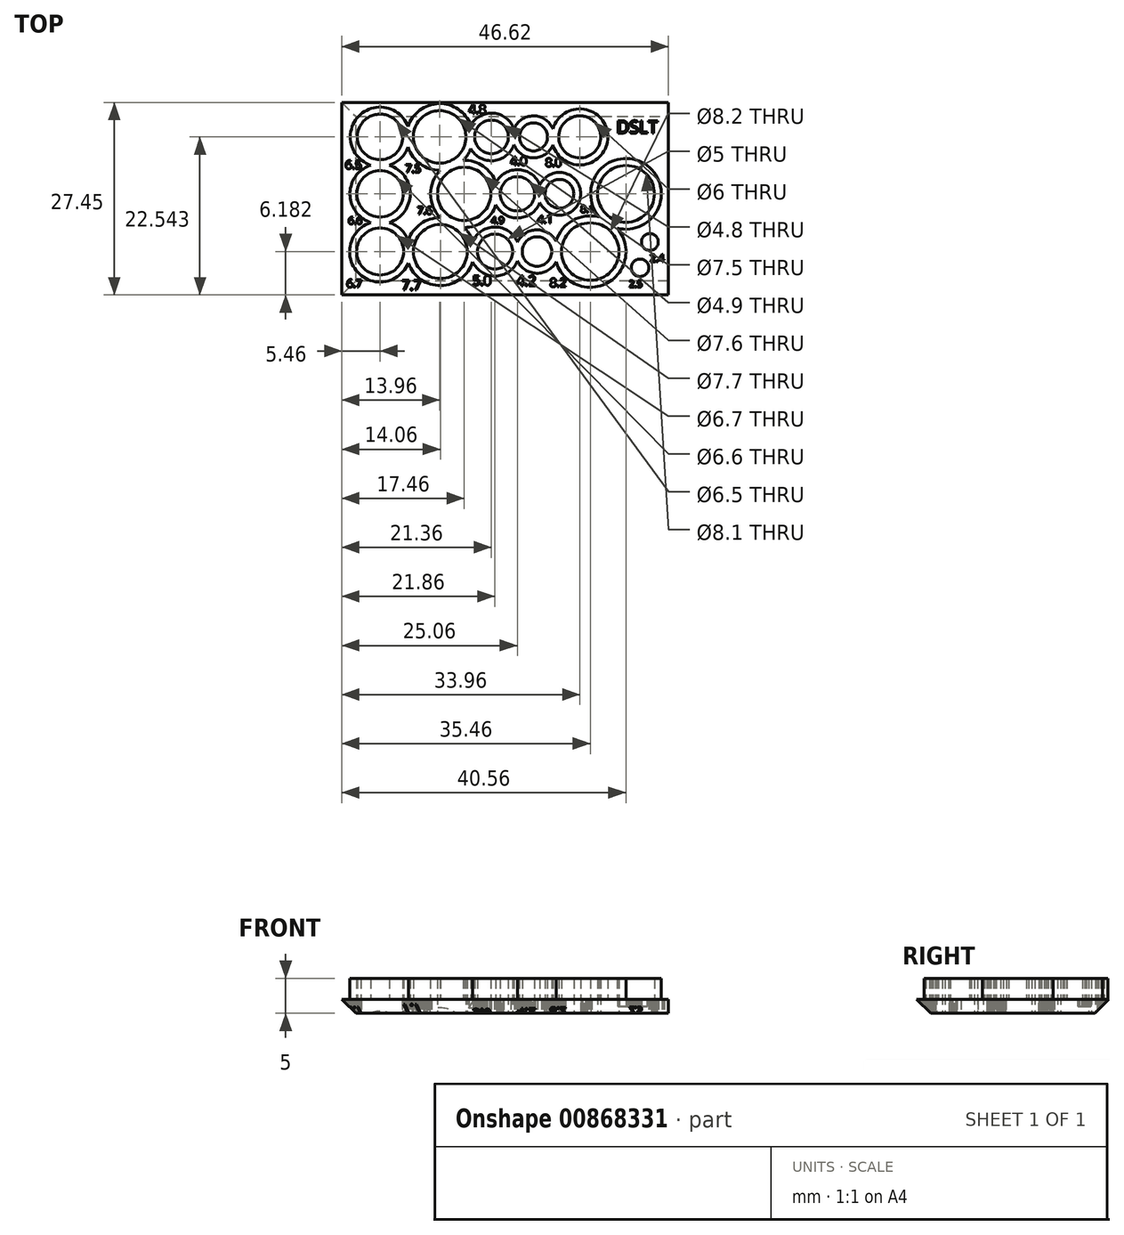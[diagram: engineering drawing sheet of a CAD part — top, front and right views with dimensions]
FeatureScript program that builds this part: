
annotation { "Feature Type Name" : "Feature", "Feature Type Description" : "" }
export const myFeature = defineFeature(function(context is Context, id is Id, definition is map)
    precondition{}
    {
        {
            var Q0;
            Q0=qCreatedBy(makeId("Top.planeOp"),FACE);
            var sketch = newSketch(context, id + "F0", { "sketchPlane" : qUnion([Q0])});
            skCircle(sketch, "E0", {"center": v(0, 0) * mm, "radius": 3.3 * mm});
            skLineSegment(sketch, "E1", {"start": v(0, 0) * mm, "end": v(43.8, 0) * mm, "construction": true});
            skLineSegment(sketch, "E2", {"start": v(0, 8.12) * mm, "end": v(43.8, 8.12) * mm, "construction": true});
            skCircle(sketch, "E3", {"center": v(0, 8.12) * mm, "radius": 3.25 * mm});
            skCircle(sketch, "E4", {"center": v(0, -8.24) * mm, "radius": 3.35 * mm});
            skLineSegment(sketch, "E5", {"start": v(0, -8.24) * mm, "end": v(43.8, -8.24) * mm, "construction": true});
            skCircle(sketch, "E6", {"center": v(12, 0) * mm, "radius": 3.8 * mm});
            skCircle(sketch, "E7", {"center": v(8.6, -8.24) * mm, "radius": 3.85 * mm});
            skCircle(sketch, "E8", {"center": v(8.5, 8.12) * mm, "radius": 3.75 * mm});
            skCircle(sketch, "E9", {"center": v(19.6, 0) * mm, "radius": 2.45 * mm});
            skCircle(sketch, "E10", {"center": v(15.9, 8.12) * mm, "radius": 2.4 * mm});
            skCircle(sketch, "E11", {"center": v(16.4, -8.24) * mm, "radius": 2.5 * mm});
            skCircle(sketch, "E12", {"center": v(25.6, 0) * mm, "radius": 2.05 * mm});
            skCircle(sketch, "E13", {"center": v(21.9, 8.12) * mm, "radius": 2 * mm});
            skCircle(sketch, "E14", {"center": v(22.4, -8.24) * mm, "radius": 2.1 * mm});
            skCircle(sketch, "E15", {"center": v(35.1, 0) * mm, "radius": 4.05 * mm});
            skCircle(sketch, "E16", {"center": v(30, -8.24) * mm, "radius": 4.1 * mm});
            skCircle(sketch, "E17", {"center": v(28.5, 8.12) * mm, "radius": 4 * mm});
            skCircle(sketch, "E18.0", {"center": v(0, 8.12) * mm, "radius": 4.25 * mm});
            skCircle(sketch, "E19.0", {"center": v(0, 0) * mm, "radius": 4.3 * mm});
            skCircle(sketch, "E20.0", {"center": v(0, -8.24) * mm, "radius": 4.35 * mm});
            skCircle(sketch, "E21.0", {"center": v(8.5, 8.12) * mm, "radius": 4.75 * mm});
            skCircle(sketch, "E22.0", {"center": v(12, 0) * mm, "radius": 4.8 * mm});
            skCircle(sketch, "E23.0", {"center": v(8.6, -8.24) * mm, "radius": 4.85 * mm});
            skCircle(sketch, "E24.0", {"center": v(15.9, 8.12) * mm, "radius": 3.4 * mm});
            skCircle(sketch, "E25.0", {"center": v(19.6, 0) * mm, "radius": 3.45 * mm});
            skCircle(sketch, "E26.0", {"center": v(16.4, -8.24) * mm, "radius": 3.5 * mm});
            skCircle(sketch, "E27.0", {"center": v(21.9, 8.12) * mm, "radius": 3 * mm});
            skCircle(sketch, "E28.0", {"center": v(25.6, 0) * mm, "radius": 3.05 * mm});
            skCircle(sketch, "E29.0", {"center": v(22.4, -8.24) * mm, "radius": 3.1 * mm});
            skCircle(sketch, "E30.0", {"center": v(30, -8.24) * mm, "radius": 5.1 * mm});
            skCircle(sketch, "E31.0", {"center": v(28.5, 8.12) * mm, "radius": 3 * mm});
            skCircle(sketch, "E32.0", {"center": v(35.1, 0) * mm, "radius": 5.05 * mm});
            skLineSegment(sketch, "E33.bottom", {"start": v(-5.46, 13.03) * mm, "end": v(41.16, 13.03) * mm});
            skLineSegment(sketch, "E33.top", {"start": v(-5.46, -14.42) * mm, "end": v(41.16, -14.42) * mm});
            skLineSegment(sketch, "E33.left", {"start": v(-5.46, 13.03) * mm, "end": v(-5.46, -14.42) * mm});
            skLineSegment(sketch, "E33.right", {"start": v(41.16, 13.03) * mm, "end": v(41.16, -14.42) * mm});
            skText(sketch, "E34", { "text": "6.6", "fontName": "OpenSans-Regular.ttf"});
            skText(sketch, "E35", { "text": "7.6", "fontName": "OpenSans-Regular.ttf"});
            skText(sketch, "E36", { "text": "4.9\n", "fontName": "OpenSans-Regular.ttf"});
            skText(sketch, "E37", { "text": "4.1", "fontName": "OpenSans-Regular.ttf"});
            skText(sketch, "E38", { "text": "8.1", "fontName": "OpenSans-Regular.ttf"});
            skText(sketch, "E39", { "text": "6.5", "fontName": "OpenSans-Regular.ttf"});
            skText(sketch, "E40", { "text": "7.5", "fontName": "OpenSans-Regular.ttf"});
            skText(sketch, "E41", { "text": "4.8", "fontName": "OpenSans-Regular.ttf"});
            skText(sketch, "E42", { "text": "4.0", "fontName": "OpenSans-Regular.ttf"});
            skText(sketch, "E43", { "text": "8.0", "fontName": "OpenSans-Regular.ttf"});
            skText(sketch, "E44", { "text": "6.7", "fontName": "OpenSans-Regular.ttf"});
            skText(sketch, "E45", { "text": "7.7", "fontName": "OpenSans-Regular.ttf"});
            skText(sketch, "E46", { "text": "5.0", "fontName": "OpenSans-Regular.ttf"});
            skText(sketch, "E47", { "text": "8.2", "fontName": "OpenSans-Regular.ttf"});
            skText(sketch, "E48", { "text": "4.2", "fontName": "OpenSans-Regular.ttf"});
            skCircle(sketch, "E49", {"center": v(37.1, -10.55) * mm, "radius": 1.25 * mm});
            skCircle(sketch, "E50", {"center": v(38.5, -6.87) * mm, "radius": 1.2 * mm});
            skText(sketch, "E51", { "text": "2.5\n", "fontName": "OpenSans-Regular.ttf"});
            skText(sketch, "E52", { "text": "2.4\n", "fontName": "OpenSans-Regular.ttf"});
            const initialGuessF0  = {"E34": [-0.00453, -0.00432, 1, 0, 0.001], "E35": [0.00531, -0.0029, 1, 0, 0.00108], "E36": [0.01582, -0.00425, 1, 0, 0.00096], "E37": [0.02247, -0.00417, 1, 0, 0.0011], "E38": [0.02863, -0.00266, 1, 0, 0.00098], "E39": [-0.00498, 0.00356, 1, 0, 0.0012], "E40": [0.0036, 0.00304, 1, 0, 0.00114], "E41": [0.01265, 0.01143, 1, 0, 0.00126], "E42": [0.0186, 0.00408, 1, 0, 0.0012], "E43": [0.02362, 0.0039, 1, 0, 0.00116], "E44": [-0.00477, -0.01334, 1, 0, 0.00112], "E45": [0.00307, -0.01373, 1, 0, 0.00145], "E46": [0.01322, -0.01303, 1, 0, 0.00135], "E47": [0.02424, -0.01327, 1, 0, 0.0012], "E48": [0.01949, -0.01311, 1, 0, 0.00142], "E51": [0.03552, -0.01333, 1, 0, 0.00098], "E52": [0.0385, -0.0097, 1, 0, 0.00107]};
            skSetInitialGuess(sketch, initialGuessF0);
            skSolve(sketch);
        }
        {
            var Q0;
            Q0=makeQuery(id+"F0.imprint","IMPRINT",FACE,{"disambiguationData":[TD([[makeQuery(id+"F0.imprint","IMPRINT",EDGE,{"derivedFrom":sQuery(id+"F0.wireOp",EDGE,"E3")}),-1.0]])]});
            var Q1;
            {var subQ0=sQuery(id+"F0.wireOp",EDGE,"E19.0");var subQ1=sQuery(id+"F0.wireOp",EDGE,"E18.0");var subQ2=makeQuery(id+"F0.imprint","INTERSECT",VERTEX,{"disambiguationData":[OD(0.0)],"derivedFrom":[subQ1,subQ0]});Q1=makeQuery(id+"F0.imprint","IMPRINT",FACE,{"disambiguationData":[TD([[makeQuery(id+"F0.imprint","IMPRINT",EDGE,{"disambiguationData":[TD([[subQ2,-1.0]])],"derivedFrom":subQ1}),1.0]])]});}
            var Q2;
            Q2=makeQuery(id+"F0.imprint","IMPRINT",FACE,{"disambiguationData":[TD([[makeQuery(id+"F0.imprint","IMPRINT",EDGE,{"derivedFrom":sQuery(id+"F0.wireOp",EDGE,"E0")}),-1.0]])]});
            var Q3;
            {var subQ0=sQuery(id+"F0.wireOp",EDGE,"E20.0");var subQ1=sQuery(id+"F0.wireOp",EDGE,"E19.0");var subQ2=makeQuery(id+"F0.imprint","INTERSECT",VERTEX,{"disambiguationData":[OD(0.0)],"derivedFrom":[subQ1,subQ0]});Q3=makeQuery(id+"F0.imprint","IMPRINT",FACE,{"disambiguationData":[TD([[makeQuery(id+"F0.imprint","IMPRINT",EDGE,{"disambiguationData":[TD([[subQ2,-1.0]])],"derivedFrom":subQ1}),1.0]])]});}
            var Q4;
            {var subQ0=sQuery(id+"F0.wireOp",EDGE,"E23.0");var subQ1=sQuery(id+"F0.wireOp",EDGE,"E20.0");var subQ2=makeQuery(id+"F0.imprint","INTERSECT",VERTEX,{"disambiguationData":[OD(0.0)],"derivedFrom":[subQ1,subQ0]});Q4=makeQuery(id+"F0.imprint","IMPRINT",FACE,{"disambiguationData":[TD([[makeQuery(id+"F0.imprint","IMPRINT",EDGE,{"disambiguationData":[TD([[subQ2,-1.0]])],"derivedFrom":subQ1}),1.0]])]});}
            var Q5;
            Q5=makeQuery(id+"F0.imprint","IMPRINT",FACE,{"disambiguationData":[TD([[makeQuery(id+"F0.imprint","IMPRINT",EDGE,{"derivedFrom":sQuery(id+"F0.wireOp",EDGE,"E7")}),-1.0]])]});
            var Q6;
            Q6=makeQuery(id+"F0.imprint","IMPRINT",FACE,{"disambiguationData":[TD([[makeQuery(id+"F0.imprint","IMPRINT",EDGE,{"derivedFrom":sQuery(id+"F0.wireOp",EDGE,"E6")}),-1.0]])]});
            var Q7;
            {var subQ0=sQuery(id+"F0.wireOp",EDGE,"E23.0");var subQ1=sQuery(id+"F0.wireOp",EDGE,"E22.0");var subQ2=makeQuery(id+"F0.imprint","INTERSECT",VERTEX,{"disambiguationData":[OD(0.0)],"derivedFrom":[subQ1,subQ0]});Q7=makeQuery(id+"F0.imprint","IMPRINT",FACE,{"disambiguationData":[TD([[makeQuery(id+"F0.imprint","IMPRINT",EDGE,{"disambiguationData":[TD([[subQ2,1.0]])],"derivedFrom":subQ1}),1.0]])]});}
            var Q8;
            {var subQ0=sQuery(id+"F0.wireOp",EDGE,"E22.0");var subQ1=sQuery(id+"F0.wireOp",EDGE,"E21.0");var subQ2=makeQuery(id+"F0.imprint","INTERSECT",VERTEX,{"disambiguationData":[OD(0.0)],"derivedFrom":[subQ1,subQ0]});Q8=makeQuery(id+"F0.imprint","IMPRINT",FACE,{"disambiguationData":[TD([[makeQuery(id+"F0.imprint","IMPRINT",EDGE,{"disambiguationData":[TD([[subQ2,1.0]])],"derivedFrom":subQ1}),1.0]])]});}
            var Q9;
            Q9=makeQuery(id+"F0.imprint","IMPRINT",FACE,{"disambiguationData":[TD([[makeQuery(id+"F0.imprint","IMPRINT",EDGE,{"derivedFrom":sQuery(id+"F0.wireOp",EDGE,"E8")}),-1.0]])]});
            var Q10;
            {var subQ0=sQuery(id+"F0.wireOp",EDGE,"E24.0");var subQ1=sQuery(id+"F0.wireOp",EDGE,"E21.0");var subQ2=makeQuery(id+"F0.imprint","INTERSECT",VERTEX,{"disambiguationData":[OD(0.0)],"derivedFrom":[subQ1,subQ0]});Q10=makeQuery(id+"F0.imprint","IMPRINT",FACE,{"disambiguationData":[TD([[makeQuery(id+"F0.imprint","IMPRINT",EDGE,{"disambiguationData":[TD([[subQ2,1.0]])],"derivedFrom":subQ1}),1.0]])]});}
            var Q11;
            Q11=makeQuery(id+"F0.imprint","IMPRINT",FACE,{"disambiguationData":[TD([[makeQuery(id+"F0.imprint","IMPRINT",EDGE,{"derivedFrom":sQuery(id+"F0.wireOp",EDGE,"E10")}),-1.0]])]});
            var Q12;
            {var subQ0=sQuery(id+"F0.wireOp",EDGE,"E27.0");var subQ1=sQuery(id+"F0.wireOp",EDGE,"E24.0");var subQ2=makeQuery(id+"F0.imprint","INTERSECT",VERTEX,{"disambiguationData":[OD(0.0)],"derivedFrom":[subQ1,subQ0]});Q12=makeQuery(id+"F0.imprint","IMPRINT",FACE,{"disambiguationData":[TD([[makeQuery(id+"F0.imprint","IMPRINT",EDGE,{"disambiguationData":[TD([[subQ2,1.0]])],"derivedFrom":subQ1}),1.0]])]});}
            var Q13;
            Q13=makeQuery(id+"F0.imprint","IMPRINT",FACE,{"disambiguationData":[TD([[makeQuery(id+"F0.imprint","IMPRINT",EDGE,{"derivedFrom":sQuery(id+"F0.wireOp",EDGE,"E13")}),-1.0]])]});
            var Q14;
            Q14=makeQuery(id+"F0.imprint","IMPRINT",FACE,{"disambiguationData":[TD([[makeQuery(id+"F0.imprint","IMPRINT",EDGE,{"derivedFrom":sQuery(id+"F0.wireOp",EDGE,"E9")}),-1.0]])]});
            var Q15;
            {var subQ0=sQuery(id+"F0.wireOp",EDGE,"E25.0");var subQ1=sQuery(id+"F0.wireOp",EDGE,"E22.0");var subQ2=makeQuery(id+"F0.imprint","INTERSECT",VERTEX,{"disambiguationData":[OD(0.0)],"derivedFrom":[subQ1,subQ0]});Q15=makeQuery(id+"F0.imprint","IMPRINT",FACE,{"disambiguationData":[TD([[makeQuery(id+"F0.imprint","IMPRINT",EDGE,{"disambiguationData":[TD([[subQ2,1.0]])],"derivedFrom":subQ1}),1.0]])]});}
            var Q16;
            {var subQ0=sQuery(id+"F0.wireOp",EDGE,"E26.0");var subQ1=sQuery(id+"F0.wireOp",EDGE,"E23.0");var subQ2=makeQuery(id+"F0.imprint","INTERSECT",VERTEX,{"disambiguationData":[OD(0.0)],"derivedFrom":[subQ1,subQ0]});Q16=makeQuery(id+"F0.imprint","IMPRINT",FACE,{"disambiguationData":[TD([[makeQuery(id+"F0.imprint","IMPRINT",EDGE,{"disambiguationData":[TD([[subQ2,1.0]])],"derivedFrom":subQ1}),1.0]])]});}
            var Q17;
            Q17=makeQuery(id+"F0.imprint","IMPRINT",FACE,{"disambiguationData":[TD([[makeQuery(id+"F0.imprint","IMPRINT",EDGE,{"derivedFrom":sQuery(id+"F0.wireOp",EDGE,"E11")}),-1.0]])]});
            var Q18;
            {var subQ0=sQuery(id+"F0.wireOp",EDGE,"E29.0");var subQ1=sQuery(id+"F0.wireOp",EDGE,"E26.0");var subQ2=makeQuery(id+"F0.imprint","INTERSECT",VERTEX,{"disambiguationData":[OD(0.0)],"derivedFrom":[subQ1,subQ0]});Q18=makeQuery(id+"F0.imprint","IMPRINT",FACE,{"disambiguationData":[TD([[makeQuery(id+"F0.imprint","IMPRINT",EDGE,{"disambiguationData":[TD([[subQ2,1.0]])],"derivedFrom":subQ1}),1.0]])]});}
            var Q19;
            Q19=makeQuery(id+"F0.imprint","IMPRINT",FACE,{"disambiguationData":[TD([[makeQuery(id+"F0.imprint","IMPRINT",EDGE,{"derivedFrom":sQuery(id+"F0.wireOp",EDGE,"E14")}),-1.0]])]});
            var Q20;
            {var subQ0=sQuery(id+"F0.wireOp",EDGE,"E28.0");var subQ1=sQuery(id+"F0.wireOp",EDGE,"E25.0");var subQ2=makeQuery(id+"F0.imprint","INTERSECT",VERTEX,{"disambiguationData":[OD(0.0)],"derivedFrom":[subQ1,subQ0]});Q20=makeQuery(id+"F0.imprint","IMPRINT",FACE,{"disambiguationData":[TD([[makeQuery(id+"F0.imprint","IMPRINT",EDGE,{"disambiguationData":[TD([[subQ2,1.0]])],"derivedFrom":subQ1}),1.0]])]});}
            var Q21;
            Q21=makeQuery(id+"F0.imprint","IMPRINT",FACE,{"disambiguationData":[TD([[makeQuery(id+"F0.imprint","IMPRINT",EDGE,{"derivedFrom":sQuery(id+"F0.wireOp",EDGE,"E12")}),-1.0]])]});
            var Q22;
            Q22=makeQuery(id+"F0.imprint","IMPRINT",FACE,{"disambiguationData":[TD([[makeQuery(id+"F0.imprint","IMPRINT",EDGE,{"derivedFrom":sQuery(id+"F0.wireOp",EDGE,"E16")}),-1.0]])]});
            var Q23;
            {var subQ0=sQuery(id+"F0.wireOp",EDGE,"E30.0");var subQ1=sQuery(id+"F0.wireOp",EDGE,"E29.0");var subQ2=makeQuery(id+"F0.imprint","INTERSECT",VERTEX,{"disambiguationData":[OD(0.0)],"derivedFrom":[subQ1,subQ0]});Q23=makeQuery(id+"F0.imprint","IMPRINT",FACE,{"disambiguationData":[TD([[makeQuery(id+"F0.imprint","IMPRINT",EDGE,{"disambiguationData":[TD([[subQ2,1.0]])],"derivedFrom":subQ1}),1.0]])]});}
            var Q24;
            {var subQ0=sQuery(id+"F0.wireOp",EDGE,"E32.0");var subQ1=sQuery(id+"F0.wireOp",EDGE,"E30.0");var subQ2=makeQuery(id+"F0.imprint","INTERSECT",VERTEX,{"disambiguationData":[OD(0.0)],"derivedFrom":[subQ1,subQ0]});Q24=makeQuery(id+"F0.imprint","IMPRINT",FACE,{"disambiguationData":[TD([[makeQuery(id+"F0.imprint","IMPRINT",EDGE,{"disambiguationData":[TD([[subQ2,1.0]])],"derivedFrom":subQ1}),1.0]])]});}
            var Q25;
            Q25=makeQuery(id+"F0.imprint","IMPRINT",FACE,{"disambiguationData":[TD([[makeQuery(id+"F0.imprint","IMPRINT",EDGE,{"derivedFrom":sQuery(id+"F0.wireOp",EDGE,"E15")}),-1.0]])]});
            var Q26;
            {var subQ0=sQuery(id+"F0.wireOp",EDGE,"E27.0");var subQ1=sQuery(id+"F0.wireOp",EDGE,"E17");var subQ2=makeQuery(id+"F0.imprint","INTERSECT",VERTEX,{"disambiguationData":[OD(0.0)],"derivedFrom":[subQ1,subQ0]});Q26=makeQuery(id+"F0.imprint","IMPRINT",FACE,{"disambiguationData":[TD([[makeQuery(id+"F0.imprint","IMPRINT",EDGE,{"disambiguationData":[TD([[subQ2,-1.0]])],"derivedFrom":subQ1}),1.0]])]});}
            var Q27;
            Q27=makeQuery(id+"F0.imprint","IMPRINT",FACE,{"disambiguationData":[TD([[makeQuery(id+"F0.imprint","IMPRINT",EDGE,{"derivedFrom":sQuery(id+"F0.wireOp",EDGE,"E31.0")}),-1.0]])]});
            var Q28;
            {var subQ0=sQuery(id+"F0.wireOp",EDGE,"E21.0");var subQ1=sQuery(id+"F0.wireOp",EDGE,"E18.0");var subQ2=makeQuery(id+"F0.imprint","INTERSECT",VERTEX,{"disambiguationData":[OD(0.0)],"derivedFrom":[subQ1,subQ0]});Q28=makeQuery(id+"F0.imprint","IMPRINT",FACE,{"disambiguationData":[TD([[makeQuery(id+"F0.imprint","IMPRINT",EDGE,{"disambiguationData":[TD([[subQ2,1.0]])],"derivedFrom":subQ1}),1.0]])]});}
            var Q29;
            Q29=makeQuery(id+"F0.imprint","IMPRINT",FACE,{"disambiguationData":[TD([[makeQuery(id+"F0.imprint","IMPRINT",EDGE,{"derivedFrom":sQuery(id+"F0.wireOp",EDGE,"E4")}),-1.0]])]});
            var Q30;
            {var subQ0=sQuery(id+"F0.wireOp",EDGE,"E23.0");var subQ1=sQuery(id+"F0.wireOp",EDGE,"E20.0");var subQ2=makeQuery(id+"F0.imprint","INTERSECT",VERTEX,{"disambiguationData":[OD(0.0)],"derivedFrom":[subQ1,subQ0]});Q30=makeQuery(id+"F0.imprint","IMPRINT",FACE,{"disambiguationData":[TD([[makeQuery(id+"F0.imprint","IMPRINT",EDGE,{"disambiguationData":[TD([[subQ2,1.0]])],"derivedFrom":subQ1}),1.0]])]});}
            var Q31;
            {var subQ0=sQuery(id+"F0.wireOp",EDGE,"E23.0");var subQ1=sQuery(id+"F0.wireOp",EDGE,"E22.0");var subQ2=makeQuery(id+"F0.imprint","INTERSECT",VERTEX,{"disambiguationData":[OD(0.0)],"derivedFrom":[subQ1,subQ0]});Q31=makeQuery(id+"F0.imprint","IMPRINT",FACE,{"disambiguationData":[TD([[makeQuery(id+"F0.imprint","IMPRINT",EDGE,{"disambiguationData":[TD([[subQ2,-1.0]])],"derivedFrom":subQ1}),1.0]])]});}
            var Q32;
            {var subQ0=sQuery(id+"F0.wireOp",EDGE,"E22.0");var subQ1=sQuery(id+"F0.wireOp",EDGE,"E21.0");var subQ2=makeQuery(id+"F0.imprint","INTERSECT",VERTEX,{"disambiguationData":[OD(0.0)],"derivedFrom":[subQ1,subQ0]});Q32=makeQuery(id+"F0.imprint","IMPRINT",FACE,{"disambiguationData":[TD([[makeQuery(id+"F0.imprint","IMPRINT",EDGE,{"disambiguationData":[TD([[subQ2,-1.0]])],"derivedFrom":subQ1}),1.0]])]});}
            extrude(context, id + "F1", {"entities" : qUnion([Q0, Q1, Q2, Q3, Q4, Q5, Q6, Q7, Q8, Q9, Q10, Q11, Q12, Q13, Q14, Q15, Q16, Q17, Q18, Q19, Q20, Q21, Q22, Q23, Q24, Q25, Q26, Q27, Q28, Q29, Q30, Q31, Q32]), "depth" : 5 * mm, "offsetDistance" : 25 * mm});
        }
        {
            var Q0;
            Q0=makeQuery(id+"F0.imprint","IMPRINT",FACE,{"disambiguationData":[TD([[makeQuery(id+"F0.imprint","IMPRINT",EDGE,{"derivedFrom":sQuery(id+"F0.wireOp",EDGE,"E33.bottom")}),-1.0]])]});
            var Q1;
            Q1=makeQuery(id+"F0.imprint","IMPRINT",FACE,{"disambiguationData":[TD([[makeQuery(id+"F0.imprint","IMPRINT",EDGE,{"derivedFrom":sQuery(id+"F0.wireOp",EDGE,"E35.sketch_text.stroke-0")}),1.0]])]});
            extrude(context, id + "F2", {"entities" : qUnion([Q0, Q1]), "operationType" : NewBodyOperationType.ADD, "depth" : 2 * mm, "offsetDistance" : 25 * mm});
        }
        {
            var Q0;
            Q0=makeQuery(id+"F2.opExtrude","CAP_FACE",FACE,{"disambiguationData":[OSD([sQuery(id+"F0.wireOp",EDGE,"E17"),sQuery(id+"F0.wireOp",EDGE,"E18.0"),sQuery(id+"F0.wireOp",EDGE,"E19.0"),sQuery(id+"F0.wireOp",EDGE,"E20.0"),sQuery(id+"F0.wireOp",EDGE,"E21.0"),sQuery(id+"F0.wireOp",EDGE,"E22.0"),sQuery(id+"F0.wireOp",EDGE,"E23.0"),sQuery(id+"F0.wireOp",EDGE,"E24.0"),sQuery(id+"F0.wireOp",EDGE,"E25.0"),sQuery(id+"F0.wireOp",EDGE,"E26.0"),sQuery(id+"F0.wireOp",EDGE,"E27.0"),sQuery(id+"F0.wireOp",EDGE,"E28.0"),sQuery(id+"F0.wireOp",EDGE,"E29.0"),sQuery(id+"F0.wireOp",EDGE,"E30.0"),sQuery(id+"F0.wireOp",EDGE,"E32.0"),sQuery(id+"F0.wireOp",EDGE,"E33.bottom"),sQuery(id+"F0.wireOp",EDGE,"E33.top"),sQuery(id+"F0.wireOp",EDGE,"E33.left"),sQuery(id+"F0.wireOp",EDGE,"E33.right"),sQuery(id+"F0.wireOp",EDGE,"E34.sketch_text.stroke-0"),sQuery(id+"F0.wireOp",EDGE,"E34.sketch_text.stroke-1"),sQuery(id+"F0.wireOp",EDGE,"E34.sketch_text.stroke-2"),sQuery(id+"F0.wireOp",EDGE,"E34.sketch_text.stroke-3"),sQuery(id+"F0.wireOp",EDGE,"E34.sketch_text.stroke-4"),sQuery(id+"F0.wireOp",EDGE,"E34.sketch_text.stroke-5"),sQuery(id+"F0.wireOp",EDGE,"E34.sketch_text.stroke-6"),sQuery(id+"F0.wireOp",EDGE,"E34.sketch_text.stroke-7"),sQuery(id+"F0.wireOp",EDGE,"E34.sketch_text.stroke-8"),sQuery(id+"F0.wireOp",EDGE,"E34.sketch_text.stroke-9"),sQuery(id+"F0.wireOp",EDGE,"E34.sketch_text.stroke-10"),sQuery(id+"F0.wireOp",EDGE,"E34.sketch_text.stroke-11"),sQuery(id+"F0.wireOp",EDGE,"E34.sketch_text.stroke-12"),sQuery(id+"F0.wireOp",EDGE,"E34.sketch_text.stroke-13"),sQuery(id+"F0.wireOp",EDGE,"E34.sketch_text.stroke-14"),sQuery(id+"F0.wireOp",EDGE,"E34.sketch_text.stroke-25"),sQuery(id+"F0.wireOp",EDGE,"E34.sketch_text.stroke-26"),sQuery(id+"F0.wireOp",EDGE,"E34.sketch_text.stroke-27"),sQuery(id+"F0.wireOp",EDGE,"E34.sketch_text.stroke-28"),sQuery(id+"F0.wireOp",EDGE,"E34.sketch_text.stroke-29"),sQuery(id+"F0.wireOp",EDGE,"E34.sketch_text.stroke-30"),sQuery(id+"F0.wireOp",EDGE,"E34.sketch_text.stroke-31"),sQuery(id+"F0.wireOp",EDGE,"E34.sketch_text.stroke-32"),sQuery(id+"F0.wireOp",EDGE,"E34.sketch_text.stroke-33"),sQuery(id+"F0.wireOp",EDGE,"E34.sketch_text.stroke-34"),sQuery(id+"F0.wireOp",EDGE,"E34.sketch_text.stroke-35"),sQuery(id+"F0.wireOp",EDGE,"E34.sketch_text.stroke-36"),sQuery(id+"F0.wireOp",EDGE,"E34.sketch_text.stroke-37"),sQuery(id+"F0.wireOp",EDGE,"E34.sketch_text.stroke-38"),sQuery(id+"F0.wireOp",EDGE,"E34.sketch_text.stroke-39"),sQuery(id+"F0.wireOp",EDGE,"E34.sketch_text.stroke-40"),sQuery(id+"F0.wireOp",EDGE,"E34.sketch_text.stroke-41"),sQuery(id+"F0.wireOp",EDGE,"E34.sketch_text.stroke-42"),sQuery(id+"F0.wireOp",EDGE,"E34.sketch_text.stroke-43"),sQuery(id+"F0.wireOp",EDGE,"E34.sketch_text.stroke-44"),sQuery(id+"F0.wireOp",EDGE,"E34.sketch_text.stroke-45"),sQuery(id+"F0.wireOp",EDGE,"E34.sketch_text.stroke-46"),sQuery(id+"F0.wireOp",EDGE,"E34.sketch_text.stroke-47"),sQuery(id+"F0.wireOp",EDGE,"E36.sketch_text.stroke-0"),sQuery(id+"F0.wireOp",EDGE,"E36.sketch_text.stroke-1"),sQuery(id+"F0.wireOp",EDGE,"E36.sketch_text.stroke-2"),sQuery(id+"F0.wireOp",EDGE,"E36.sketch_text.stroke-3"),sQuery(id+"F0.wireOp",EDGE,"E36.sketch_text.stroke-4"),sQuery(id+"F0.wireOp",EDGE,"E36.sketch_text.stroke-5"),sQuery(id+"F0.wireOp",EDGE,"E36.sketch_text.stroke-6"),sQuery(id+"F0.wireOp",EDGE,"E36.sketch_text.stroke-7"),sQuery(id+"F0.wireOp",EDGE,"E36.sketch_text.stroke-8"),sQuery(id+"F0.wireOp",EDGE,"E36.sketch_text.stroke-9"),sQuery(id+"F0.wireOp",EDGE,"E36.sketch_text.stroke-10"),sQuery(id+"F0.wireOp",EDGE,"E36.sketch_text.stroke-17"),sQuery(id+"F0.wireOp",EDGE,"E36.sketch_text.stroke-18"),sQuery(id+"F0.wireOp",EDGE,"E36.sketch_text.stroke-19"),sQuery(id+"F0.wireOp",EDGE,"E36.sketch_text.stroke-20"),sQuery(id+"F0.wireOp",EDGE,"E36.sketch_text.stroke-21"),sQuery(id+"F0.wireOp",EDGE,"E36.sketch_text.stroke-22"),sQuery(id+"F0.wireOp",EDGE,"E36.sketch_text.stroke-23"),sQuery(id+"F0.wireOp",EDGE,"E36.sketch_text.stroke-24"),sQuery(id+"F0.wireOp",EDGE,"E36.sketch_text.stroke-25"),sQuery(id+"F0.wireOp",EDGE,"E36.sketch_text.stroke-26"),sQuery(id+"F0.wireOp",EDGE,"E36.sketch_text.stroke-27"),sQuery(id+"F0.wireOp",EDGE,"E36.sketch_text.stroke-28"),sQuery(id+"F0.wireOp",EDGE,"E36.sketch_text.stroke-29"),sQuery(id+"F0.wireOp",EDGE,"E36.sketch_text.stroke-30"),sQuery(id+"F0.wireOp",EDGE,"E36.sketch_text.stroke-31"),sQuery(id+"F0.wireOp",EDGE,"E36.sketch_text.stroke-32"),sQuery(id+"F0.wireOp",EDGE,"E36.sketch_text.stroke-33"),sQuery(id+"F0.wireOp",EDGE,"E36.sketch_text.stroke-34"),sQuery(id+"F0.wireOp",EDGE,"E36.sketch_text.stroke-35"),sQuery(id+"F0.wireOp",EDGE,"E36.sketch_text.stroke-36"),sQuery(id+"F0.wireOp",EDGE,"E36.sketch_text.stroke-37"),sQuery(id+"F0.wireOp",EDGE,"E36.sketch_text.stroke-38"),sQuery(id+"F0.wireOp",EDGE,"E36.sketch_text.stroke-39"),sQuery(id+"F0.wireOp",EDGE,"E36.sketch_text.stroke-40"),sQuery(id+"F0.wireOp",EDGE,"E37.sketch_text.stroke-0"),sQuery(id+"F0.wireOp",EDGE,"E37.sketch_text.stroke-1"),sQuery(id+"F0.wireOp",EDGE,"E37.sketch_text.stroke-2"),sQuery(id+"F0.wireOp",EDGE,"E37.sketch_text.stroke-3"),sQuery(id+"F0.wireOp",EDGE,"E37.sketch_text.stroke-4"),sQuery(id+"F0.wireOp",EDGE,"E37.sketch_text.stroke-5"),sQuery(id+"F0.wireOp",EDGE,"E37.sketch_text.stroke-6"),sQuery(id+"F0.wireOp",EDGE,"E37.sketch_text.stroke-7"),sQuery(id+"F0.wireOp",EDGE,"E37.sketch_text.stroke-8"),sQuery(id+"F0.wireOp",EDGE,"E37.sketch_text.stroke-9"),sQuery(id+"F0.wireOp",EDGE,"E37.sketch_text.stroke-10"),sQuery(id+"F0.wireOp",EDGE,"E37.sketch_text.stroke-17"),sQuery(id+"F0.wireOp",EDGE,"E37.sketch_text.stroke-18"),sQuery(id+"F0.wireOp",EDGE,"E37.sketch_text.stroke-19"),sQuery(id+"F0.wireOp",EDGE,"E37.sketch_text.stroke-20"),sQuery(id+"F0.wireOp",EDGE,"E37.sketch_text.stroke-21"),sQuery(id+"F0.wireOp",EDGE,"E37.sketch_text.stroke-22"),sQuery(id+"F0.wireOp",EDGE,"E37.sketch_text.stroke-23"),sQuery(id+"F0.wireOp",EDGE,"E37.sketch_text.stroke-24"),sQuery(id+"F0.wireOp",EDGE,"E37.sketch_text.stroke-25"),sQuery(id+"F0.wireOp",EDGE,"E37.sketch_text.stroke-26"),sQuery(id+"F0.wireOp",EDGE,"E37.sketch_text.stroke-27"),sQuery(id+"F0.wireOp",EDGE,"E37.sketch_text.stroke-28"),sQuery(id+"F0.wireOp",EDGE,"E37.sketch_text.stroke-29"),sQuery(id+"F0.wireOp",EDGE,"E37.sketch_text.stroke-30"),sQuery(id+"F0.wireOp",EDGE,"E37.sketch_text.stroke-31"),sQuery(id+"F0.wireOp",EDGE,"E37.sketch_text.stroke-32"),sQuery(id+"F0.wireOp",EDGE,"E37.sketch_text.stroke-33"),sQuery(id+"F0.wireOp",EDGE,"E38.sketch_text.stroke-0"),sQuery(id+"F0.wireOp",EDGE,"E38.sketch_text.stroke-1"),sQuery(id+"F0.wireOp",EDGE,"E38.sketch_text.stroke-2"),sQuery(id+"F0.wireOp",EDGE,"E38.sketch_text.stroke-3"),sQuery(id+"F0.wireOp",EDGE,"E38.sketch_text.stroke-4"),sQuery(id+"F0.wireOp",EDGE,"E38.sketch_text.stroke-5"),sQuery(id+"F0.wireOp",EDGE,"E38.sketch_text.stroke-6"),sQuery(id+"F0.wireOp",EDGE,"E38.sketch_text.stroke-7"),sQuery(id+"F0.wireOp",EDGE,"E38.sketch_text.stroke-8"),sQuery(id+"F0.wireOp",EDGE,"E38.sketch_text.stroke-9"),sQuery(id+"F0.wireOp",EDGE,"E38.sketch_text.stroke-10"),sQuery(id+"F0.wireOp",EDGE,"E38.sketch_text.stroke-11"),sQuery(id+"F0.wireOp",EDGE,"E38.sketch_text.stroke-12"),sQuery(id+"F0.wireOp",EDGE,"E38.sketch_text.stroke-13"),sQuery(id+"F0.wireOp",EDGE,"E38.sketch_text.stroke-14"),sQuery(id+"F0.wireOp",EDGE,"E38.sketch_text.stroke-31"),sQuery(id+"F0.wireOp",EDGE,"E38.sketch_text.stroke-32"),sQuery(id+"F0.wireOp",EDGE,"E38.sketch_text.stroke-33"),sQuery(id+"F0.wireOp",EDGE,"E38.sketch_text.stroke-34"),sQuery(id+"F0.wireOp",EDGE,"E38.sketch_text.stroke-35"),sQuery(id+"F0.wireOp",EDGE,"E38.sketch_text.stroke-36"),sQuery(id+"F0.wireOp",EDGE,"E38.sketch_text.stroke-37"),sQuery(id+"F0.wireOp",EDGE,"E38.sketch_text.stroke-38"),sQuery(id+"F0.wireOp",EDGE,"E38.sketch_text.stroke-39"),sQuery(id+"F0.wireOp",EDGE,"E38.sketch_text.stroke-40"),sQuery(id+"F0.wireOp",EDGE,"E38.sketch_text.stroke-41"),sQuery(id+"F0.wireOp",EDGE,"E38.sketch_text.stroke-42"),sQuery(id+"F0.wireOp",EDGE,"E38.sketch_text.stroke-43"),sQuery(id+"F0.wireOp",EDGE,"E38.sketch_text.stroke-44"),sQuery(id+"F0.wireOp",EDGE,"E38.sketch_text.stroke-45"),sQuery(id+"F0.wireOp",EDGE,"E38.sketch_text.stroke-46"),sQuery(id+"F0.wireOp",EDGE,"E38.sketch_text.stroke-47"),sQuery(id+"F0.wireOp",EDGE,"E39.sketch_text.stroke-0"),sQuery(id+"F0.wireOp",EDGE,"E39.sketch_text.stroke-1"),sQuery(id+"F0.wireOp",EDGE,"E39.sketch_text.stroke-2"),sQuery(id+"F0.wireOp",EDGE,"E39.sketch_text.stroke-3"),sQuery(id+"F0.wireOp",EDGE,"E39.sketch_text.stroke-4"),sQuery(id+"F0.wireOp",EDGE,"E39.sketch_text.stroke-5"),sQuery(id+"F0.wireOp",EDGE,"E39.sketch_text.stroke-6"),sQuery(id+"F0.wireOp",EDGE,"E39.sketch_text.stroke-7"),sQuery(id+"F0.wireOp",EDGE,"E39.sketch_text.stroke-8"),sQuery(id+"F0.wireOp",EDGE,"E39.sketch_text.stroke-9"),sQuery(id+"F0.wireOp",EDGE,"E39.sketch_text.stroke-10"),sQuery(id+"F0.wireOp",EDGE,"E39.sketch_text.stroke-11"),sQuery(id+"F0.wireOp",EDGE,"E39.sketch_text.stroke-12"),sQuery(id+"F0.wireOp",EDGE,"E39.sketch_text.stroke-13"),sQuery(id+"F0.wireOp",EDGE,"E39.sketch_text.stroke-14"),sQuery(id+"F0.wireOp",EDGE,"E39.sketch_text.stroke-25"),sQuery(id+"F0.wireOp",EDGE,"E39.sketch_text.stroke-26"),sQuery(id+"F0.wireOp",EDGE,"E39.sketch_text.stroke-27"),sQuery(id+"F0.wireOp",EDGE,"E39.sketch_text.stroke-28"),sQuery(id+"F0.wireOp",EDGE,"E39.sketch_text.stroke-29"),sQuery(id+"F0.wireOp",EDGE,"E39.sketch_text.stroke-30"),sQuery(id+"F0.wireOp",EDGE,"E39.sketch_text.stroke-31"),sQuery(id+"F0.wireOp",EDGE,"E39.sketch_text.stroke-32"),sQuery(id+"F0.wireOp",EDGE,"E39.sketch_text.stroke-33"),sQuery(id+"F0.wireOp",EDGE,"E39.sketch_text.stroke-34"),sQuery(id+"F0.wireOp",EDGE,"E39.sketch_text.stroke-35"),sQuery(id+"F0.wireOp",EDGE,"E39.sketch_text.stroke-36"),sQuery(id+"F0.wireOp",EDGE,"E39.sketch_text.stroke-37"),sQuery(id+"F0.wireOp",EDGE,"E39.sketch_text.stroke-38"),sQuery(id+"F0.wireOp",EDGE,"E39.sketch_text.stroke-39"),sQuery(id+"F0.wireOp",EDGE,"E39.sketch_text.stroke-40"),sQuery(id+"F0.wireOp",EDGE,"E39.sketch_text.stroke-41"),sQuery(id+"F0.wireOp",EDGE,"E39.sketch_text.stroke-42"),sQuery(id+"F0.wireOp",EDGE,"E39.sketch_text.stroke-43"),sQuery(id+"F0.wireOp",EDGE,"E39.sketch_text.stroke-44"),sQuery(id+"F0.wireOp",EDGE,"E39.sketch_text.stroke-45"),sQuery(id+"F0.wireOp",EDGE,"E39.sketch_text.stroke-46"),sQuery(id+"F0.wireOp",EDGE,"E39.sketch_text.stroke-47"),sQuery(id+"F0.wireOp",EDGE,"E39.sketch_text.stroke-48"),sQuery(id+"F0.wireOp",EDGE,"E39.sketch_text.stroke-49"),sQuery(id+"F0.wireOp",EDGE,"E39.sketch_text.stroke-50"),sQuery(id+"F0.wireOp",EDGE,"E39.sketch_text.stroke-51"),sQuery(id+"F0.wireOp",EDGE,"E41.sketch_text.stroke-0"),sQuery(id+"F0.wireOp",EDGE,"E41.sketch_text.stroke-1"),sQuery(id+"F0.wireOp",EDGE,"E41.sketch_text.stroke-2"),sQuery(id+"F0.wireOp",EDGE,"E41.sketch_text.stroke-3"),sQuery(id+"F0.wireOp",EDGE,"E41.sketch_text.stroke-4"),sQuery(id+"F0.wireOp",EDGE,"E41.sketch_text.stroke-5"),sQuery(id+"F0.wireOp",EDGE,"E41.sketch_text.stroke-6"),sQuery(id+"F0.wireOp",EDGE,"E41.sketch_text.stroke-7"),sQuery(id+"F0.wireOp",EDGE,"E41.sketch_text.stroke-8"),sQuery(id+"F0.wireOp",EDGE,"E41.sketch_text.stroke-9"),sQuery(id+"F0.wireOp",EDGE,"E41.sketch_text.stroke-10"),sQuery(id+"F0.wireOp",EDGE,"E41.sketch_text.stroke-17"),sQuery(id+"F0.wireOp",EDGE,"E41.sketch_text.stroke-18"),sQuery(id+"F0.wireOp",EDGE,"E41.sketch_text.stroke-19"),sQuery(id+"F0.wireOp",EDGE,"E41.sketch_text.stroke-20"),sQuery(id+"F0.wireOp",EDGE,"E41.sketch_text.stroke-21"),sQuery(id+"F0.wireOp",EDGE,"E41.sketch_text.stroke-22"),sQuery(id+"F0.wireOp",EDGE,"E41.sketch_text.stroke-23"),sQuery(id+"F0.wireOp",EDGE,"E41.sketch_text.stroke-24"),sQuery(id+"F0.wireOp",EDGE,"E41.sketch_text.stroke-25"),sQuery(id+"F0.wireOp",EDGE,"E41.sketch_text.stroke-26"),sQuery(id+"F0.wireOp",EDGE,"E41.sketch_text.stroke-27"),sQuery(id+"F0.wireOp",EDGE,"E41.sketch_text.stroke-28"),sQuery(id+"F0.wireOp",EDGE,"E41.sketch_text.stroke-29"),sQuery(id+"F0.wireOp",EDGE,"E41.sketch_text.stroke-30"),sQuery(id+"F0.wireOp",EDGE,"E41.sketch_text.stroke-31"),sQuery(id+"F0.wireOp",EDGE,"E41.sketch_text.stroke-32"),sQuery(id+"F0.wireOp",EDGE,"E41.sketch_text.stroke-33"),sQuery(id+"F0.wireOp",EDGE,"E41.sketch_text.stroke-34"),sQuery(id+"F0.wireOp",EDGE,"E41.sketch_text.stroke-35"),sQuery(id+"F0.wireOp",EDGE,"E41.sketch_text.stroke-36"),sQuery(id+"F0.wireOp",EDGE,"E41.sketch_text.stroke-37"),sQuery(id+"F0.wireOp",EDGE,"E41.sketch_text.stroke-38"),sQuery(id+"F0.wireOp",EDGE,"E41.sketch_text.stroke-39"),sQuery(id+"F0.wireOp",EDGE,"E42.sketch_text.stroke-0"),sQuery(id+"F0.wireOp",EDGE,"E42.sketch_text.stroke-1"),sQuery(id+"F0.wireOp",EDGE,"E42.sketch_text.stroke-2"),sQuery(id+"F0.wireOp",EDGE,"E42.sketch_text.stroke-3"),sQuery(id+"F0.wireOp",EDGE,"E42.sketch_text.stroke-4"),sQuery(id+"F0.wireOp",EDGE,"E42.sketch_text.stroke-5"),sQuery(id+"F0.wireOp",EDGE,"E42.sketch_text.stroke-6"),sQuery(id+"F0.wireOp",EDGE,"E42.sketch_text.stroke-7"),sQuery(id+"F0.wireOp",EDGE,"E42.sketch_text.stroke-8"),sQuery(id+"F0.wireOp",EDGE,"E42.sketch_text.stroke-9"),sQuery(id+"F0.wireOp",EDGE,"E42.sketch_text.stroke-10"),sQuery(id+"F0.wireOp",EDGE,"E42.sketch_text.stroke-17"),sQuery(id+"F0.wireOp",EDGE,"E42.sketch_text.stroke-18"),sQuery(id+"F0.wireOp",EDGE,"E42.sketch_text.stroke-19"),sQuery(id+"F0.wireOp",EDGE,"E42.sketch_text.stroke-20"),sQuery(id+"F0.wireOp",EDGE,"E42.sketch_text.stroke-21"),sQuery(id+"F0.wireOp",EDGE,"E42.sketch_text.stroke-22"),sQuery(id+"F0.wireOp",EDGE,"E42.sketch_text.stroke-23"),sQuery(id+"F0.wireOp",EDGE,"E42.sketch_text.stroke-24"),sQuery(id+"F0.wireOp",EDGE,"E42.sketch_text.stroke-25"),sQuery(id+"F0.wireOp",EDGE,"E42.sketch_text.stroke-26"),sQuery(id+"F0.wireOp",EDGE,"E42.sketch_text.stroke-27"),sQuery(id+"F0.wireOp",EDGE,"E42.sketch_text.stroke-28"),sQuery(id+"F0.wireOp",EDGE,"E42.sketch_text.stroke-29"),sQuery(id+"F0.wireOp",EDGE,"E42.sketch_text.stroke-30"),sQuery(id+"F0.wireOp",EDGE,"E42.sketch_text.stroke-31"),sQuery(id+"F0.wireOp",EDGE,"E42.sketch_text.stroke-32"),sQuery(id+"F0.wireOp",EDGE,"E43.sketch_text.stroke-0"),sQuery(id+"F0.wireOp",EDGE,"E43.sketch_text.stroke-1"),sQuery(id+"F0.wireOp",EDGE,"E43.sketch_text.stroke-2"),sQuery(id+"F0.wireOp",EDGE,"E43.sketch_text.stroke-3"),sQuery(id+"F0.wireOp",EDGE,"E43.sketch_text.stroke-4"),sQuery(id+"F0.wireOp",EDGE,"E43.sketch_text.stroke-5"),sQuery(id+"F0.wireOp",EDGE,"E43.sketch_text.stroke-6"),sQuery(id+"F0.wireOp",EDGE,"E43.sketch_text.stroke-7"),sQuery(id+"F0.wireOp",EDGE,"E43.sketch_text.stroke-8"),sQuery(id+"F0.wireOp",EDGE,"E43.sketch_text.stroke-9"),sQuery(id+"F0.wireOp",EDGE,"E43.sketch_text.stroke-10"),sQuery(id+"F0.wireOp",EDGE,"E43.sketch_text.stroke-11"),sQuery(id+"F0.wireOp",EDGE,"E43.sketch_text.stroke-12"),sQuery(id+"F0.wireOp",EDGE,"E43.sketch_text.stroke-13"),sQuery(id+"F0.wireOp",EDGE,"E43.sketch_text.stroke-14"),sQuery(id+"F0.wireOp",EDGE,"E43.sketch_text.stroke-31"),sQuery(id+"F0.wireOp",EDGE,"E43.sketch_text.stroke-32"),sQuery(id+"F0.wireOp",EDGE,"E43.sketch_text.stroke-33"),sQuery(id+"F0.wireOp",EDGE,"E43.sketch_text.stroke-34"),sQuery(id+"F0.wireOp",EDGE,"E43.sketch_text.stroke-35"),sQuery(id+"F0.wireOp",EDGE,"E43.sketch_text.stroke-36"),sQuery(id+"F0.wireOp",EDGE,"E43.sketch_text.stroke-37"),sQuery(id+"F0.wireOp",EDGE,"E43.sketch_text.stroke-38"),sQuery(id+"F0.wireOp",EDGE,"E43.sketch_text.stroke-39"),sQuery(id+"F0.wireOp",EDGE,"E43.sketch_text.stroke-40"),sQuery(id+"F0.wireOp",EDGE,"E43.sketch_text.stroke-41"),sQuery(id+"F0.wireOp",EDGE,"E43.sketch_text.stroke-42"),sQuery(id+"F0.wireOp",EDGE,"E43.sketch_text.stroke-43"),sQuery(id+"F0.wireOp",EDGE,"E43.sketch_text.stroke-44"),sQuery(id+"F0.wireOp",EDGE,"E43.sketch_text.stroke-45"),sQuery(id+"F0.wireOp",EDGE,"E43.sketch_text.stroke-46"),sQuery(id+"F0.wireOp",EDGE,"E44.sketch_text.stroke-0"),sQuery(id+"F0.wireOp",EDGE,"E44.sketch_text.stroke-1"),sQuery(id+"F0.wireOp",EDGE,"E44.sketch_text.stroke-2"),sQuery(id+"F0.wireOp",EDGE,"E44.sketch_text.stroke-3"),sQuery(id+"F0.wireOp",EDGE,"E44.sketch_text.stroke-4"),sQuery(id+"F0.wireOp",EDGE,"E44.sketch_text.stroke-5"),sQuery(id+"F0.wireOp",EDGE,"E44.sketch_text.stroke-6"),sQuery(id+"F0.wireOp",EDGE,"E44.sketch_text.stroke-7"),sQuery(id+"F0.wireOp",EDGE,"E44.sketch_text.stroke-8"),sQuery(id+"F0.wireOp",EDGE,"E44.sketch_text.stroke-9"),sQuery(id+"F0.wireOp",EDGE,"E44.sketch_text.stroke-10"),sQuery(id+"F0.wireOp",EDGE,"E44.sketch_text.stroke-11"),sQuery(id+"F0.wireOp",EDGE,"E44.sketch_text.stroke-12"),sQuery(id+"F0.wireOp",EDGE,"E44.sketch_text.stroke-13"),sQuery(id+"F0.wireOp",EDGE,"E44.sketch_text.stroke-14"),sQuery(id+"F0.wireOp",EDGE,"E44.sketch_text.stroke-25"),sQuery(id+"F0.wireOp",EDGE,"E44.sketch_text.stroke-26"),sQuery(id+"F0.wireOp",EDGE,"E44.sketch_text.stroke-27"),sQuery(id+"F0.wireOp",EDGE,"E44.sketch_text.stroke-28"),sQuery(id+"F0.wireOp",EDGE,"E44.sketch_text.stroke-29"),sQuery(id+"F0.wireOp",EDGE,"E44.sketch_text.stroke-30"),sQuery(id+"F0.wireOp",EDGE,"E44.sketch_text.stroke-31"),sQuery(id+"F0.wireOp",EDGE,"E44.sketch_text.stroke-32"),sQuery(id+"F0.wireOp",EDGE,"E44.sketch_text.stroke-33"),sQuery(id+"F0.wireOp",EDGE,"E44.sketch_text.stroke-34"),sQuery(id+"F0.wireOp",EDGE,"E44.sketch_text.stroke-35"),sQuery(id+"F0.wireOp",EDGE,"E44.sketch_text.stroke-36"),sQuery(id+"F0.wireOp",EDGE,"E44.sketch_text.stroke-37"),sQuery(id+"F0.wireOp",EDGE,"E44.sketch_text.stroke-38"),sQuery(id+"F0.wireOp",EDGE,"E44.sketch_text.stroke-39"),sQuery(id+"F0.wireOp",EDGE,"E45.sketch_text.stroke-0"),sQuery(id+"F0.wireOp",EDGE,"E45.sketch_text.stroke-1"),sQuery(id+"F0.wireOp",EDGE,"E45.sketch_text.stroke-2"),sQuery(id+"F0.wireOp",EDGE,"E45.sketch_text.stroke-3"),sQuery(id+"F0.wireOp",EDGE,"E45.sketch_text.stroke-4"),sQuery(id+"F0.wireOp",EDGE,"E45.sketch_text.stroke-5"),sQuery(id+"F0.wireOp",EDGE,"E45.sketch_text.stroke-6"),sQuery(id+"F0.wireOp",EDGE,"E45.sketch_text.stroke-7"),sQuery(id+"F0.wireOp",EDGE,"E45.sketch_text.stroke-8"),sQuery(id+"F0.wireOp",EDGE,"E45.sketch_text.stroke-9"),sQuery(id+"F0.wireOp",EDGE,"E45.sketch_text.stroke-10"),sQuery(id+"F0.wireOp",EDGE,"E45.sketch_text.stroke-11"),sQuery(id+"F0.wireOp",EDGE,"E45.sketch_text.stroke-12"),sQuery(id+"F0.wireOp",EDGE,"E45.sketch_text.stroke-13"),sQuery(id+"F0.wireOp",EDGE,"E45.sketch_text.stroke-14"),sQuery(id+"F0.wireOp",EDGE,"E45.sketch_text.stroke-15"),sQuery(id+"F0.wireOp",EDGE,"E45.sketch_text.stroke-16"),sQuery(id+"F0.wireOp",EDGE,"E45.sketch_text.stroke-17"),sQuery(id+"F0.wireOp",EDGE,"E45.sketch_text.stroke-18"),sQuery(id+"F0.wireOp",EDGE,"E45.sketch_text.stroke-19"),sQuery(id+"F0.wireOp",EDGE,"E45.sketch_text.stroke-20"),sQuery(id+"F0.wireOp",EDGE,"E45.sketch_text.stroke-21"),sQuery(id+"F0.wireOp",EDGE,"E46.sketch_text.stroke-0"),sQuery(id+"F0.wireOp",EDGE,"E46.sketch_text.stroke-1"),sQuery(id+"F0.wireOp",EDGE,"E46.sketch_text.stroke-2"),sQuery(id+"F0.wireOp",EDGE,"E46.sketch_text.stroke-3"),sQuery(id+"F0.wireOp",EDGE,"E46.sketch_text.stroke-4"),sQuery(id+"F0.wireOp",EDGE,"E46.sketch_text.stroke-5"),sQuery(id+"F0.wireOp",EDGE,"E46.sketch_text.stroke-6"),sQuery(id+"F0.wireOp",EDGE,"E46.sketch_text.stroke-7"),sQuery(id+"F0.wireOp",EDGE,"E46.sketch_text.stroke-8"),sQuery(id+"F0.wireOp",EDGE,"E46.sketch_text.stroke-9"),sQuery(id+"F0.wireOp",EDGE,"E46.sketch_text.stroke-10"),sQuery(id+"F0.wireOp",EDGE,"E46.sketch_text.stroke-11"),sQuery(id+"F0.wireOp",EDGE,"E46.sketch_text.stroke-12"),sQuery(id+"F0.wireOp",EDGE,"E46.sketch_text.stroke-13"),sQuery(id+"F0.wireOp",EDGE,"E46.sketch_text.stroke-14"),sQuery(id+"F0.wireOp",EDGE,"E46.sketch_text.stroke-15"),sQuery(id+"F0.wireOp",EDGE,"E46.sketch_text.stroke-16"),sQuery(id+"F0.wireOp",EDGE,"E46.sketch_text.stroke-17"),sQuery(id+"F0.wireOp",EDGE,"E46.sketch_text.stroke-18"),sQuery(id+"F0.wireOp",EDGE,"E46.sketch_text.stroke-19"),sQuery(id+"F0.wireOp",EDGE,"E46.sketch_text.stroke-20"),sQuery(id+"F0.wireOp",EDGE,"E46.sketch_text.stroke-21"),sQuery(id+"F0.wireOp",EDGE,"E46.sketch_text.stroke-22"),sQuery(id+"F0.wireOp",EDGE,"E46.sketch_text.stroke-23"),sQuery(id+"F0.wireOp",EDGE,"E46.sketch_text.stroke-24"),sQuery(id+"F0.wireOp",EDGE,"E46.sketch_text.stroke-25"),sQuery(id+"F0.wireOp",EDGE,"E46.sketch_text.stroke-26"),sQuery(id+"F0.wireOp",EDGE,"E46.sketch_text.stroke-27"),sQuery(id+"F0.wireOp",EDGE,"E46.sketch_text.stroke-28"),sQuery(id+"F0.wireOp",EDGE,"E46.sketch_text.stroke-29"),sQuery(id+"F0.wireOp",EDGE,"E46.sketch_text.stroke-30"),sQuery(id+"F0.wireOp",EDGE,"E46.sketch_text.stroke-31"),sQuery(id+"F0.wireOp",EDGE,"E46.sketch_text.stroke-32"),sQuery(id+"F0.wireOp",EDGE,"E46.sketch_text.stroke-33"),sQuery(id+"F0.wireOp",EDGE,"E46.sketch_text.stroke-34"),sQuery(id+"F0.wireOp",EDGE,"E47.sketch_text.stroke-0"),sQuery(id+"F0.wireOp",EDGE,"E47.sketch_text.stroke-1"),sQuery(id+"F0.wireOp",EDGE,"E47.sketch_text.stroke-2"),sQuery(id+"F0.wireOp",EDGE,"E47.sketch_text.stroke-3"),sQuery(id+"F0.wireOp",EDGE,"E47.sketch_text.stroke-4"),sQuery(id+"F0.wireOp",EDGE,"E47.sketch_text.stroke-5"),sQuery(id+"F0.wireOp",EDGE,"E47.sketch_text.stroke-6"),sQuery(id+"F0.wireOp",EDGE,"E47.sketch_text.stroke-7"),sQuery(id+"F0.wireOp",EDGE,"E47.sketch_text.stroke-8"),sQuery(id+"F0.wireOp",EDGE,"E47.sketch_text.stroke-9"),sQuery(id+"F0.wireOp",EDGE,"E47.sketch_text.stroke-10"),sQuery(id+"F0.wireOp",EDGE,"E47.sketch_text.stroke-11"),sQuery(id+"F0.wireOp",EDGE,"E47.sketch_text.stroke-12"),sQuery(id+"F0.wireOp",EDGE,"E47.sketch_text.stroke-13"),sQuery(id+"F0.wireOp",EDGE,"E47.sketch_text.stroke-14"),sQuery(id+"F0.wireOp",EDGE,"E47.sketch_text.stroke-31"),sQuery(id+"F0.wireOp",EDGE,"E47.sketch_text.stroke-32"),sQuery(id+"F0.wireOp",EDGE,"E47.sketch_text.stroke-33"),sQuery(id+"F0.wireOp",EDGE,"E47.sketch_text.stroke-34"),sQuery(id+"F0.wireOp",EDGE,"E47.sketch_text.stroke-35"),sQuery(id+"F0.wireOp",EDGE,"E47.sketch_text.stroke-36"),sQuery(id+"F0.wireOp",EDGE,"E47.sketch_text.stroke-37"),sQuery(id+"F0.wireOp",EDGE,"E47.sketch_text.stroke-38"),sQuery(id+"F0.wireOp",EDGE,"E47.sketch_text.stroke-39"),sQuery(id+"F0.wireOp",EDGE,"E47.sketch_text.stroke-40"),sQuery(id+"F0.wireOp",EDGE,"E47.sketch_text.stroke-41"),sQuery(id+"F0.wireOp",EDGE,"E47.sketch_text.stroke-42"),sQuery(id+"F0.wireOp",EDGE,"E47.sketch_text.stroke-43"),sQuery(id+"F0.wireOp",EDGE,"E47.sketch_text.stroke-44"),sQuery(id+"F0.wireOp",EDGE,"E47.sketch_text.stroke-45"),sQuery(id+"F0.wireOp",EDGE,"E47.sketch_text.stroke-46"),sQuery(id+"F0.wireOp",EDGE,"E47.sketch_text.stroke-47"),sQuery(id+"F0.wireOp",EDGE,"E47.sketch_text.stroke-48"),sQuery(id+"F0.wireOp",EDGE,"E47.sketch_text.stroke-49"),sQuery(id+"F0.wireOp",EDGE,"E47.sketch_text.stroke-50"),sQuery(id+"F0.wireOp",EDGE,"E47.sketch_text.stroke-51"),sQuery(id+"F0.wireOp",EDGE,"E47.sketch_text.stroke-52"),sQuery(id+"F0.wireOp",EDGE,"E47.sketch_text.stroke-53"),sQuery(id+"F0.wireOp",EDGE,"E47.sketch_text.stroke-54"),sQuery(id+"F0.wireOp",EDGE,"E47.sketch_text.stroke-55"),sQuery(id+"F0.wireOp",EDGE,"E47.sketch_text.stroke-56"),sQuery(id+"F0.wireOp",EDGE,"E47.sketch_text.stroke-57"),sQuery(id+"F0.wireOp",EDGE,"E47.sketch_text.stroke-58"),sQuery(id+"F0.wireOp",EDGE,"E48.sketch_text.stroke-0"),sQuery(id+"F0.wireOp",EDGE,"E48.sketch_text.stroke-1"),sQuery(id+"F0.wireOp",EDGE,"E48.sketch_text.stroke-2"),sQuery(id+"F0.wireOp",EDGE,"E48.sketch_text.stroke-3"),sQuery(id+"F0.wireOp",EDGE,"E48.sketch_text.stroke-4"),sQuery(id+"F0.wireOp",EDGE,"E48.sketch_text.stroke-5"),sQuery(id+"F0.wireOp",EDGE,"E48.sketch_text.stroke-6"),sQuery(id+"F0.wireOp",EDGE,"E48.sketch_text.stroke-7"),sQuery(id+"F0.wireOp",EDGE,"E48.sketch_text.stroke-8"),sQuery(id+"F0.wireOp",EDGE,"E48.sketch_text.stroke-9"),sQuery(id+"F0.wireOp",EDGE,"E48.sketch_text.stroke-10"),sQuery(id+"F0.wireOp",EDGE,"E48.sketch_text.stroke-17"),sQuery(id+"F0.wireOp",EDGE,"E48.sketch_text.stroke-18"),sQuery(id+"F0.wireOp",EDGE,"E48.sketch_text.stroke-19"),sQuery(id+"F0.wireOp",EDGE,"E48.sketch_text.stroke-20"),sQuery(id+"F0.wireOp",EDGE,"E48.sketch_text.stroke-21"),sQuery(id+"F0.wireOp",EDGE,"E48.sketch_text.stroke-22"),sQuery(id+"F0.wireOp",EDGE,"E48.sketch_text.stroke-23"),sQuery(id+"F0.wireOp",EDGE,"E48.sketch_text.stroke-24"),sQuery(id+"F0.wireOp",EDGE,"E48.sketch_text.stroke-25"),sQuery(id+"F0.wireOp",EDGE,"E48.sketch_text.stroke-26"),sQuery(id+"F0.wireOp",EDGE,"E48.sketch_text.stroke-27"),sQuery(id+"F0.wireOp",EDGE,"E48.sketch_text.stroke-28"),sQuery(id+"F0.wireOp",EDGE,"E48.sketch_text.stroke-29"),sQuery(id+"F0.wireOp",EDGE,"E48.sketch_text.stroke-30"),sQuery(id+"F0.wireOp",EDGE,"E48.sketch_text.stroke-31"),sQuery(id+"F0.wireOp",EDGE,"E48.sketch_text.stroke-32"),sQuery(id+"F0.wireOp",EDGE,"E48.sketch_text.stroke-33"),sQuery(id+"F0.wireOp",EDGE,"E48.sketch_text.stroke-34"),sQuery(id+"F0.wireOp",EDGE,"E48.sketch_text.stroke-35"),sQuery(id+"F0.wireOp",EDGE,"E48.sketch_text.stroke-36"),sQuery(id+"F0.wireOp",EDGE,"E48.sketch_text.stroke-37"),sQuery(id+"F0.wireOp",EDGE,"E48.sketch_text.stroke-38"),sQuery(id+"F0.wireOp",EDGE,"E48.sketch_text.stroke-39"),sQuery(id+"F0.wireOp",EDGE,"E48.sketch_text.stroke-40"),sQuery(id+"F0.wireOp",EDGE,"E48.sketch_text.stroke-41"),sQuery(id+"F0.wireOp",EDGE,"E48.sketch_text.stroke-42"),sQuery(id+"F0.wireOp",EDGE,"E48.sketch_text.stroke-43"),sQuery(id+"F0.wireOp",EDGE,"E48.sketch_text.stroke-44"),sQuery(id+"F0.wireOp",EDGE,"E49"),sQuery(id+"F0.wireOp",EDGE,"E50"),sQuery(id+"F0.wireOp",EDGE,"E51.sketch_text.stroke-0"),sQuery(id+"F0.wireOp",EDGE,"E51.sketch_text.stroke-1"),sQuery(id+"F0.wireOp",EDGE,"E51.sketch_text.stroke-2"),sQuery(id+"F0.wireOp",EDGE,"E51.sketch_text.stroke-3"),sQuery(id+"F0.wireOp",EDGE,"E51.sketch_text.stroke-4"),sQuery(id+"F0.wireOp",EDGE,"E51.sketch_text.stroke-5"),sQuery(id+"F0.wireOp",EDGE,"E51.sketch_text.stroke-6"),sQuery(id+"F0.wireOp",EDGE,"E51.sketch_text.stroke-7"),sQuery(id+"F0.wireOp",EDGE,"E51.sketch_text.stroke-8"),sQuery(id+"F0.wireOp",EDGE,"E51.sketch_text.stroke-9"),sQuery(id+"F0.wireOp",EDGE,"E51.sketch_text.stroke-10"),sQuery(id+"F0.wireOp",EDGE,"E51.sketch_text.stroke-11"),sQuery(id+"F0.wireOp",EDGE,"E51.sketch_text.stroke-12"),sQuery(id+"F0.wireOp",EDGE,"E51.sketch_text.stroke-13"),sQuery(id+"F0.wireOp",EDGE,"E51.sketch_text.stroke-14"),sQuery(id+"F0.wireOp",EDGE,"E51.sketch_text.stroke-15"),sQuery(id+"F0.wireOp",EDGE,"E51.sketch_text.stroke-16"),sQuery(id+"F0.wireOp",EDGE,"E51.sketch_text.stroke-17"),sQuery(id+"F0.wireOp",EDGE,"E51.sketch_text.stroke-18"),sQuery(id+"F0.wireOp",EDGE,"E51.sketch_text.stroke-19"),sQuery(id+"F0.wireOp",EDGE,"E51.sketch_text.stroke-20"),sQuery(id+"F0.wireOp",EDGE,"E51.sketch_text.stroke-21"),sQuery(id+"F0.wireOp",EDGE,"E51.sketch_text.stroke-22"),sQuery(id+"F0.wireOp",EDGE,"E51.sketch_text.stroke-23"),sQuery(id+"F0.wireOp",EDGE,"E51.sketch_text.stroke-24"),sQuery(id+"F0.wireOp",EDGE,"E51.sketch_text.stroke-25"),sQuery(id+"F0.wireOp",EDGE,"E51.sketch_text.stroke-26"),sQuery(id+"F0.wireOp",EDGE,"E51.sketch_text.stroke-27"),sQuery(id+"F0.wireOp",EDGE,"E51.sketch_text.stroke-28"),sQuery(id+"F0.wireOp",EDGE,"E51.sketch_text.stroke-29"),sQuery(id+"F0.wireOp",EDGE,"E51.sketch_text.stroke-30"),sQuery(id+"F0.wireOp",EDGE,"E51.sketch_text.stroke-31"),sQuery(id+"F0.wireOp",EDGE,"E51.sketch_text.stroke-32"),sQuery(id+"F0.wireOp",EDGE,"E51.sketch_text.stroke-33"),sQuery(id+"F0.wireOp",EDGE,"E51.sketch_text.stroke-34"),sQuery(id+"F0.wireOp",EDGE,"E51.sketch_text.stroke-35"),sQuery(id+"F0.wireOp",EDGE,"E51.sketch_text.stroke-36"),sQuery(id+"F0.wireOp",EDGE,"E51.sketch_text.stroke-37"),sQuery(id+"F0.wireOp",EDGE,"E51.sketch_text.stroke-38"),sQuery(id+"F0.wireOp",EDGE,"E51.sketch_text.stroke-39"),sQuery(id+"F0.wireOp",EDGE,"E51.sketch_text.stroke-40"),sQuery(id+"F0.wireOp",EDGE,"E51.sketch_text.stroke-41"),sQuery(id+"F0.wireOp",EDGE,"E51.sketch_text.stroke-42"),sQuery(id+"F0.wireOp",EDGE,"E51.sketch_text.stroke-43"),sQuery(id+"F0.wireOp",EDGE,"E51.sketch_text.stroke-44"),sQuery(id+"F0.wireOp",EDGE,"E51.sketch_text.stroke-45"),sQuery(id+"F0.wireOp",EDGE,"E51.sketch_text.stroke-46"),sQuery(id+"F0.wireOp",EDGE,"E52.sketch_text.stroke-0"),sQuery(id+"F0.wireOp",EDGE,"E52.sketch_text.stroke-1"),sQuery(id+"F0.wireOp",EDGE,"E52.sketch_text.stroke-2"),sQuery(id+"F0.wireOp",EDGE,"E52.sketch_text.stroke-3"),sQuery(id+"F0.wireOp",EDGE,"E52.sketch_text.stroke-4"),sQuery(id+"F0.wireOp",EDGE,"E52.sketch_text.stroke-5"),sQuery(id+"F0.wireOp",EDGE,"E52.sketch_text.stroke-6"),sQuery(id+"F0.wireOp",EDGE,"E52.sketch_text.stroke-7"),sQuery(id+"F0.wireOp",EDGE,"E52.sketch_text.stroke-8"),sQuery(id+"F0.wireOp",EDGE,"E52.sketch_text.stroke-9"),sQuery(id+"F0.wireOp",EDGE,"E52.sketch_text.stroke-10"),sQuery(id+"F0.wireOp",EDGE,"E52.sketch_text.stroke-11"),sQuery(id+"F0.wireOp",EDGE,"E52.sketch_text.stroke-12"),sQuery(id+"F0.wireOp",EDGE,"E52.sketch_text.stroke-13"),sQuery(id+"F0.wireOp",EDGE,"E52.sketch_text.stroke-14"),sQuery(id+"F0.wireOp",EDGE,"E52.sketch_text.stroke-15"),sQuery(id+"F0.wireOp",EDGE,"E52.sketch_text.stroke-16"),sQuery(id+"F0.wireOp",EDGE,"E52.sketch_text.stroke-17"),sQuery(id+"F0.wireOp",EDGE,"E52.sketch_text.stroke-18"),sQuery(id+"F0.wireOp",EDGE,"E52.sketch_text.stroke-19"),sQuery(id+"F0.wireOp",EDGE,"E52.sketch_text.stroke-20"),sQuery(id+"F0.wireOp",EDGE,"E52.sketch_text.stroke-21"),sQuery(id+"F0.wireOp",EDGE,"E52.sketch_text.stroke-22"),sQuery(id+"F0.wireOp",EDGE,"E52.sketch_text.stroke-23"),sQuery(id+"F0.wireOp",EDGE,"E52.sketch_text.stroke-24"),sQuery(id+"F0.wireOp",EDGE,"E52.sketch_text.stroke-25"),sQuery(id+"F0.wireOp",EDGE,"E52.sketch_text.stroke-26"),sQuery(id+"F0.wireOp",EDGE,"E52.sketch_text.stroke-27"),sQuery(id+"F0.wireOp",EDGE,"E52.sketch_text.stroke-28"),sQuery(id+"F0.wireOp",EDGE,"E52.sketch_text.stroke-29"),sQuery(id+"F0.wireOp",EDGE,"E52.sketch_text.stroke-30"),sQuery(id+"F0.wireOp",EDGE,"E52.sketch_text.stroke-31"),sQuery(id+"F0.wireOp",EDGE,"E52.sketch_text.stroke-32"),sQuery(id+"F0.wireOp",EDGE,"E52.sketch_text.stroke-33"),sQuery(id+"F0.wireOp",EDGE,"E52.sketch_text.stroke-34"),sQuery(id+"F0.wireOp",EDGE,"E52.sketch_text.stroke-35"),sQuery(id+"F0.wireOp",EDGE,"E52.sketch_text.stroke-36"),sQuery(id+"F0.wireOp",EDGE,"E52.sketch_text.stroke-37"),sQuery(id+"F0.wireOp",EDGE,"E52.sketch_text.stroke-38")])],"isStart":false});
            var sketch = newSketch(context, id + "F3", { "sketchPlane" : qUnion([Q0])});
            skText(sketch, "E53", { "text": "DSLT", "fontName": "OpenSans-Regular.ttf"});
            const initialGuessF3  = {"E53": [0.03375, 0.00865, 1, 0, 0.0018]};
            skSetInitialGuess(sketch, initialGuessF3);
            skSolve(sketch);
        }
        {
            var Q0;
            Q0 = qSketchRegion(id + "F3", true);
            extrude(context, id + "F4", {"entities" : qUnion([Q0]), "operationType" : NewBodyOperationType.REMOVE, "oppositeDirection" : true, "depth" : 1 * mm, "offsetDistance" : 25 * mm});
        }
        {
            var Q0;
            Q0=makeQuery(id+"F2.opExtrude","CAP_EDGE",EDGE,{"disambiguationData":[OSD([sQuery(id+"F0.wireOp",EDGE,"E33.top")])],"isStart":true});
            var Q1;
            Q1=makeQuery(id+"F2.opExtrude","CAP_EDGE",EDGE,{"disambiguationData":[OSD([sQuery(id+"F0.wireOp",EDGE,"E33.left")])],"isStart":true});
            var Q2;
            Q2=makeQuery(id+"F2.opExtrude","CAP_EDGE",EDGE,{"disambiguationData":[OSD([sQuery(id+"F0.wireOp",EDGE,"E33.bottom")])],"isStart":true});
            chamfer(context, id + "F5", {"entities" : qUnion([Q0, Q1, Q2]), "width" : 2 * mm, "tangentPropagation" : true});
        }
    });
